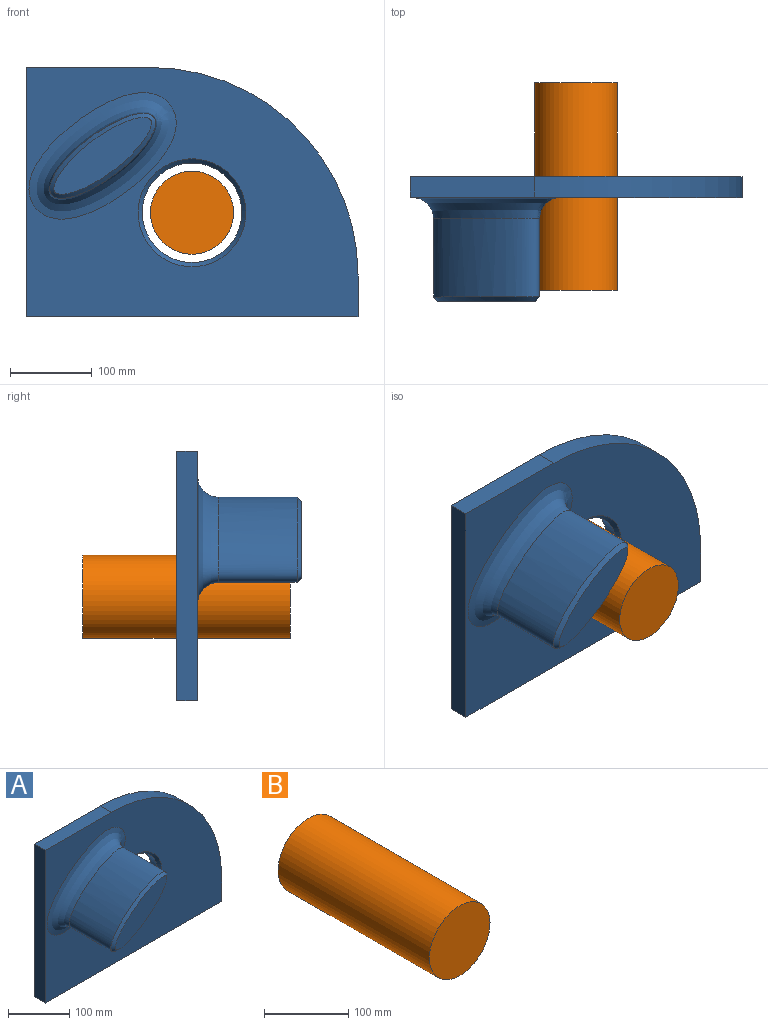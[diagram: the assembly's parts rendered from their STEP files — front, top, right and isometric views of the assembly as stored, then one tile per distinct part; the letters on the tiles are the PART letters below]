
ASSEMBLY  parts=2 mates=1
PART A: 14 faces, bbox 407.8x153.8x306.2 mm
  f0: plane 304.8x25.4mm, normal (-1,0,0), area 7741.9mm2, adj f1,f3,f5,f6
  f1: plane 406.4x25.4mm, normal (0,0,-1), area 10322.6mm2, adj f0,f2,f5,f6
  f2: plane 50.8x25.4mm, normal (1,0,0), area 1290.3mm2, adj f1,f5,f6,f7
  f3: plane 152.4x25.4mm, normal (0,0,1), area 3871mm2, adj f0,f5,f6,f7
  f4: cylinder r=60.9mm len=121.8mm, axis (0,1,0), area 5831.6mm2, adj f12,f13
  f5: plane 406.4x304.8mm, normal (0,-1,0), area 78660.9mm2, adj f0,f1,f2,f3,f7,f10,f13
  f6: plane 406.4x304.8mm, normal (0,1,0), area 96348.8mm2, adj f0,f1,f2,f3,f7,f12
  f7: cylinder r=254mm len=254mm, axis (0,-1,0), area 10134.1mm2, adj f2,f3,f5,f6
  f8: extruded ~129.23x104mm, area 33973mm2, adj f10,f11
  f9: plane 121.04x95.45mm, normal (0,-1,0), area 5106.3mm2, adj f11
  f10: bspline ~180.3x154.96mm, area 16347.2mm2, adj f5,f8
  f11: bspline ~129.13x103.89mm, area 2413.5mm2, adj f8,f9
  f12: cone r=65.98mm half-angle=45deg, axis (0,1,0), area 2863.7mm2, adj f4,f6
  f13: cone r=60.9mm half-angle=45deg, axis (0,-1,0), area 2863.7mm2, adj f4,f5
PART B: 3 faces, bbox 101.6x254x101.6 mm
  f0: cylinder r=50.8mm len=254mm, axis (0,1,0), area 81073.2mm2, adj f1,f2
  f1: plane 101.6x101.6mm, normal (0,-1,0), area 8107.3mm2, adj f0
  f2: plane 101.6x101.6mm, normal (0,1,0), area 8107.3mm2, adj f0
PLACE A t=(-203.2,-241.3,-137.77)mm fixed
PLACE B t=(0,-126.43,-10.77)mm
MATE cylindrical A.f4 <-> B.f0  axis (0,1,0) through (0,-254,-10.77)mm
